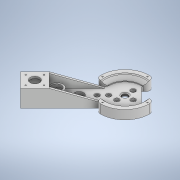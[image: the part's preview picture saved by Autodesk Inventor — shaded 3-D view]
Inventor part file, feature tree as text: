
AUTODESK INVENTOR PART (.ipt)
format: ipt  version: 2021 (Build 250183000, 183)  size: 480,768 bytes
history: native  units: mm
features: extrude x22, sketch x22, chamfer x5, fillet x3
ambient origin geometry x8: Origin, YZ Plane, XZ Plane, XY Plane, X Axis, Y Axis, Z Axis, Center Point
bodies: Solid1 (feature_tree)
feature tree (52):
  extrude  "Extrusion1"  Depth=10.0mm TaperAngle=0.0deg
  extrude  "Extrusion2"  Depth=10.0mm TaperAngle=0.0deg
  extrude  "Extrusion3"  Depth=8.0mm TaperAngle=0.0deg
  fillet  "Fillet1"  Radius=2.0mm
  chamfer  "Chamfer1"  Distance=8.0mm Angle=45.0deg
  extrude  "Extrusion4"  Depth=3.1mm
  extrude  "Extrusion5"  Depth=3.1mm
  extrude  "Extrusion6"  TaperAngle=0.0deg  [1 undecoded]
  fillet  "Fillet2"  [1 undecoded]
  extrude  "Extrusion7"  Depth=55.0mm
  extrude  "Extrusion8"  Depth=55.0mm
  chamfer  "Chamfer2"  Distance=2.0mm
  extrude  "Extrusion9"  Depth=5.5mm
  extrude  "Extrusion10"  Depth=5.5mm
  fillet  "Fillet3"  Radius=5.0mm
  extrude  "Extrusion11"  Depth=25.0mm
  chamfer  "Chamfer3"  Distance=7.0mm
  extrude  "Extrusion12"  Depth=7.0mm TaperAngle=0.0deg
  extrude  "Extrusion13"  Depth=4.1mm
  extrude  "Extrusion14"  Depth=4.1mm
  extrude  "Extrusion15"  TaperAngle=0.0deg  [1 undecoded]
  extrude  "Extrusion16"  TaperAngle=0.0deg  [1 undecoded]
  extrude  "Extrusion17"  TaperAngle=0.0deg  [1 undecoded]
  extrude  "Extrusion18"  Depth=40.0mm
  extrude  "Extrusion19"  Depth=10.0mm
  extrude  "Extrusion20"  Depth=40.0mm
  chamfer  "Chamfer4"  Distance=20.0mm
  chamfer  "Chamfer5"  Distance=7.0mm
  extrude  "Extrusion21"  Depth=10.0mm
  extrude  "Extrusion22"  Depth=10.0mm
  sketch  "Sketch1"  dims[d0=120.0mm d1=10.0mm d2=0.0mm]
  sketch  "Sketch2"  dims[d3=80.0mm d4=10.0mm d5=0.0mm]
  sketch  "Sketch3"  dims[d6=100.0mm d7=2.0mm d8=0.0mm d9=2.0mm d10=8.0mm d11=2.0mm d12=45.0deg]
  sketch  "Sketch4"  dims[d13=3.1mm d14=3.1mm]
  sketch  "Sketch5"  dims[d15=3.1mm d16=3.1mm]
  sketch  "Sketch6"  dims[d17=0.0mm d18=0.0mm d19=0.0mm]
  sketch  "Sketch7"  dims[d20=55.0mm d21=55.0mm]
  sketch  "Sketch8"  dims[d22=55.0mm d23=55.0mm]
  sketch  "Sketch10"  dims[d24=0.0mm d25=2.0mm d26=0.0mm]
  sketch  "Sketch12"  dims[d27=5.5mm d28=5.5mm]
  sketch  "Sketch13"  dims[d29=5.5mm d30=5.5mm d31=5.0mm d32=0.0mm]
  sketch  "Sketch14"  dims[d33=25.0mm d34=25.0mm]
  sketch  "Sketch15"  dims[d35=45.0deg]
  sketch  "Sketch16"  dims[d36=25.0mm]
  sketch  "Sketch17"  dims[d37=0.0mm]
  sketch  "Sketch18"  dims[d38=10.0mm]
  sketch  "Sketch19"  dims[d39=22.4mm d40=7.0mm d41=0.0mm]
  sketch  "Sketch20"  dims[d42=14.0mm d43=7.0mm d44=0.0mm]
  sketch  "Sketch21"  dims[d45=2.0mm d46=2.0mm d47=45.0deg d48=4.1mm]
  sketch  "Sketch23"  dims[d49=4.1mm d50=4.1mm]
  sketch  "Sketch24"  dims[d51=4.1mm d52=0.0mm]
  sketch  "Sketch25"  dims[d53=0.0mm d54=0.0mm d55=0.0mm d56=40.0mm d57=20.0mm d58=40.0mm d59=20.0mm d60=7.0mm d61=0.0mm d62=4.1mm d63=20.0mm d64=20.0mm d65=4.1mm d66=20.0mm d67=10.0mm d68=10.0mm d69=10.0mm d70=60.0mm d71=7.0mm d72=0.0mm d73=3.0mm d74=10.0mm d75=10.0mm d76=10.0mm d77=10.0mm d78=10.0mm d79=5.0mm d80=0.0mm d81=1.0mm d82=2.0mm d83=45.0deg d84=10.0mm d85=10.0mm d86=60.0mm d87=22.3mm d88=79.5mm d89=22.3mm d90=38.5mm d91=23.0mm d92=38.0mm d93=25.0mm d94=10.0mm d95=0.0mm d97=14.0mm d98=14.0mm d99=3.0mm d100=0.0mm d101=14.0mm d102=30.0mm d103=9.0mm d104=0.0mm d105=22.3mm d106=7.0mm d107=0.0mm d108=14.0mm d109=3.0mm d110=0.0mm d111=42.7mm d112=42.7mm d113=3.65mm d114=21.35mm d115=21.35mm d116=32.0mm d117=0.0mm d118=5.0mm d119=0.0mm d120=10.0mm d121=0.0mm d122=3.2mm d123=3.2mm d124=3.2mm d125=3.2mm d126=31.5mm d127=31.5mm d128=31.5mm d129=31.5mm d130=5.6mm d131=5.6mm d132=5.6mm d133=5.6mm d134=10.0mm d135=0.0mm d136=2.0mm d137=2.0mm d138=45.0deg d139=2.0mm d140=2.0mm d141=45.0deg d142=5.0mm d143=5.0mm d144=10.0mm d145=0.0mm d146=10.0mm d147=0.0mm d96=0.5mm]
note: 5 required parameter values undecoded (feature->parameter linkage not recoverable at this tier; creation-order binding heuristic only, values carry confidence <= 0.55)
